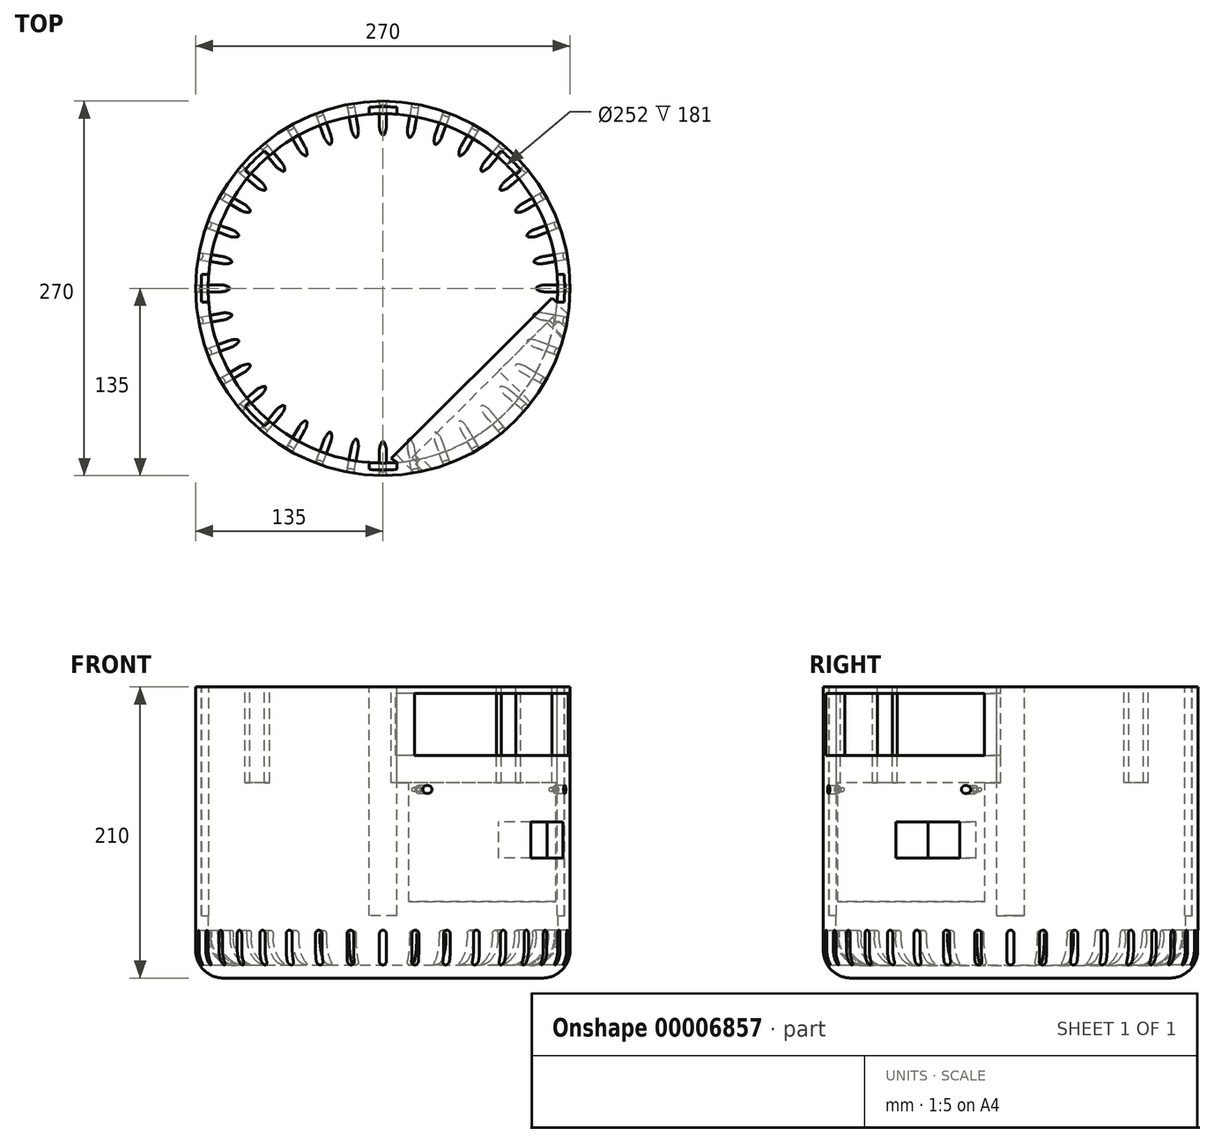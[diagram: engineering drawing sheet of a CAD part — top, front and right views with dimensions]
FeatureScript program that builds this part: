
annotation { "Feature Type Name" : "Feature", "Feature Type Description" : "" }
export const myFeature = defineFeature(function(context is Context, id is Id, definition is map)
    precondition{}
    {
        {
            var Q0;
            Q0=qCreatedBy(makeId("Top.planeOp"),FACE);
            var sketch = newSketch(context, id + "F0", { "sketchPlane" : qUnion([Q0])});
            skCircle(sketch, "E0", {"center": v(0, 0) * mm, "radius": 126 * mm});
            skCircle(sketch, "E1", {"center": v(0, 0) * mm, "radius": 135 * mm});
            skSolve(sketch);
        }
        {
            var Q0;
            Q0 = qSketchRegion(id + "F0", true);
            var Q1;
            Q1=makeQuery(id+"F0.imprint","IMPRINT",FACE,{"disambiguationData":[TD([[makeQuery(id+"F0.imprint","IMPRINT",EDGE,{"derivedFrom":sQuery(id+"F0.wireOp",EDGE,"ITGFbY2j-F6Gs-mvNy-kfQ0-MyUqCA95ELIB")}),-1.0]])]});
            var Q2;
            Q2=makeQuery(id+"F0.imprint","IMPRINT",FACE,{"disambiguationData":[TD([[makeQuery(id+"F0.imprint","IMPRINT",EDGE,{"derivedFrom":sQuery(id+"F0.wireOp",EDGE,"ITGFbY2j-F6Gs-mvNy-kfQ0-MyUqCA95ELIB")}),1.0]])]});
            var Q3;
            Q3=makeQuery(id+"F0.imprint","IMPRINT",FACE,{"disambiguationData":[TD([[makeQuery(id+"F0.imprint","IMPRINT",EDGE,{"derivedFrom":sQuery(id+"F0.wireOp",EDGE,"E0")}),1.0]])]});
            extrude(context, id + "F1", {"entities" : qUnion([Q0, Q1, Q2, Q3]), "oppositeDirection" : true, "depth" : 30 * mm});
        }
        {
            var Q0;
            Q0=makeQuery(id+"F0.imprint","IMPRINT",FACE,{"disambiguationData":[TD([[makeQuery(id+"F0.imprint","IMPRINT",EDGE,{"derivedFrom":sQuery(id+"F0.wireOp",EDGE,"E0")}),-1.0]])]});
            extrude(context, id + "F2", {"entities" : qUnion([Q0]), "operationType" : NewBodyOperationType.ADD, "depth" : 180 * mm});
        }
        {
            var Q0;
            Q0=makeQuery(id+"F1.opExtrude","CAP_FACE",FACE,{"disambiguationData":[OSD([sQuery(id+"F0.wireOp",EDGE,"E1")])],"isStart":true});
            shell(context, id + "F3", {"entities" : qUnion([Q0]), "thickness" : 9 * mm});
        }
        {
            var Q0;
            Q0=makeQuery(id+"F2.opExtrude","CAP_FACE",FACE,{"disambiguationData":[OSD([sQuery(id+"F0.wireOp",EDGE,"E0"),sQuery(id+"F0.wireOp",EDGE,"E1")])],"isStart":false});
            var sketch = newSketch(context, id + "F4", { "sketchPlane" : qUnion([Q0])});
            skCircle(sketch, "E2", {"center": v(0, 0) * mm, "radius": 126 * mm});
            skCircle(sketch, "E3", {"center": v(0, 0) * mm, "radius": 131 * mm});
            skLineSegment(sketch, "E4", {"start": v(-130.62, -10) * mm, "end": v(-125.6, -10) * mm});
            skLineSegment(sketch, "E5", {"start": v(-130.62, 10) * mm, "end": v(-125.6, 10) * mm});
            skLineSegment(sketch, "E6", {"start": v(125.6, 10) * mm, "end": v(130.62, 10) * mm});
            skLineSegment(sketch, "E7", {"start": v(125.6, -10) * mm, "end": v(130.62, -10) * mm});
            skLineSegment(sketch, "E8", {"start": v(-10, 125.6) * mm, "end": v(-10, 130.62) * mm});
            skLineSegment(sketch, "E9", {"start": v(10, 125.6) * mm, "end": v(10, 130.62) * mm});
            skPoint(sketch, "E10", {"position": v(0, 126) * mm});
            skPoint(sketch, "E11", {"position": v(-126, 0) * mm});
            skPoint(sketch, "E12", {"position": v(126, 0) * mm});
            skPoint(sketch, "E13", {"position": v(0, -126) * mm});
            skLineSegment(sketch, "E14", {"start": v(-128.11, 10) * mm, "end": v(-128.11, -10) * mm});
            skPoint(sketch, "E15", {"position": v(-128.11, 0) * mm});
            skLineSegment(sketch, "E16", {"start": v(164.04, 10) * mm, "end": v(164.04, -10) * mm});
            skPoint(sketch, "E17", {"position": v(164.04, 0) * mm});
            skLineSegment(sketch, "E18", {"start": v(-10, -125.6) * mm, "end": v(-10, -130.62) * mm});
            skLineSegment(sketch, "E19", {"start": v(10, -125.6) * mm, "end": v(10, -130.62) * mm});
            skLineSegment(sketch, "E20", {"start": v(-10, -126.16) * mm, "end": v(10, -126.16) * mm});
            skPoint(sketch, "E21", {"position": v(0, -126.16) * mm});
            skLineSegment(sketch, "E22", {"start": v(-10, 175.22) * mm, "end": v(10, 175.22) * mm});
            skPoint(sketch, "E23", {"position": v(0, 175.22) * mm});
            skLineSegment(sketch, "E24", {"start": v(0, 0) * mm, "end": v(0, 71.25) * mm});
            skLineSegment(sketch, "E25", {"start": v(23.85, 0) * mm, "end": v(0, 0) * mm});
            skLineSegment(sketch, "E26", {"start": v(-90.59, 90.59) * mm, "end": v(90.59, -90.59) * mm});
            skLineSegment(sketch, "E27", {"start": v(-43.26, -43.26) * mm, "end": v(90.59, 90.59) * mm});
            skLineSegment(sketch, "E28", {"start": v(81.74, 95.89) * mm, "end": v(85.29, 99.43) * mm});
            skLineSegment(sketch, "E29", {"start": v(95.89, 81.74) * mm, "end": v(99.43, 85.29) * mm});
            skLineSegment(sketch, "E30", {"start": v(83.52, 97.66) * mm, "end": v(97.66, 83.52) * mm});
            skPoint(sketch, "E31", {"position": v(90.59, 90.59) * mm});
            skLineSegment(sketch, "E32", {"start": v(-99.43, -85.29) * mm, "end": v(-95.89, -81.74) * mm});
            skLineSegment(sketch, "E33", {"start": v(-85.29, -99.43) * mm, "end": v(-81.74, -95.89) * mm});
            skLineSegment(sketch, "E34", {"start": v(-50.33, -36.19) * mm, "end": v(-36.19, -50.33) * mm});
            skPoint(sketch, "E35", {"position": v(-43.26, -43.26) * mm});
            skLineSegment(sketch, "E36", {"start": v(95.89, -81.74) * mm, "end": v(99.43, -85.29) * mm});
            skLineSegment(sketch, "E37", {"start": v(81.74, -95.89) * mm, "end": v(85.29, -99.43) * mm});
            skLineSegment(sketch, "E38", {"start": v(83.52, -97.66) * mm, "end": v(97.66, -83.52) * mm});
            skPoint(sketch, "E39", {"position": v(90.59, -90.59) * mm});
            skLineSegment(sketch, "E40", {"start": v(-85.29, 99.43) * mm, "end": v(-81.74, 95.89) * mm});
            skLineSegment(sketch, "E41", {"start": v(-99.43, 85.29) * mm, "end": v(-95.89, 81.74) * mm});
            skLineSegment(sketch, "E42", {"start": v(-97.66, 83.52) * mm, "end": v(-83.52, 97.66) * mm});
            skPoint(sketch, "E43", {"position": v(-90.59, 90.59) * mm});
            skSolve(sketch);
        }
        {
            var Q0;
            {var subQ5=sQuery(id+"F4.wireOp",EDGE,"E14");Q0=makeQuery(id+"F4.imprint","IMPRINT",FACE,{"disambiguationData":[TD([[makeQuery(id+"F4.imprint","IMPRINT",EDGE,{"derivedFrom":subQ5}),-1.0]])]});}
            var Q1;
            {var subQ5=sQuery(id+"F4.wireOp",EDGE,"E14");Q1=makeQuery(id+"F4.imprint","IMPRINT",FACE,{"disambiguationData":[TD([[makeQuery(id+"F4.imprint","IMPRINT",EDGE,{"derivedFrom":subQ5}),1.0]])]});}
            var Q2;
            {var subQ5=sQuery(id+"F4.wireOp",EDGE,"E22");Q2=makeQuery(id+"F4.imprint","IMPRINT",FACE,{"disambiguationData":[TD([[makeQuery(id+"F4.imprint","IMPRINT",EDGE,{"derivedFrom":subQ5}),-1.0]])]});}
            var Q3;
            {var subQ5=sQuery(id+"F4.wireOp",EDGE,"E22");Q3=makeQuery(id+"F4.imprint","IMPRINT",FACE,{"disambiguationData":[TD([[makeQuery(id+"F4.imprint","IMPRINT",EDGE,{"derivedFrom":subQ5}),1.0]])]});}
            var Q4;
            {var subQ5=sQuery(id+"F4.wireOp",EDGE,"E16");Q4=makeQuery(id+"F4.imprint","IMPRINT",FACE,{"disambiguationData":[TD([[makeQuery(id+"F4.imprint","IMPRINT",EDGE,{"derivedFrom":subQ5}),1.0]])]});}
            var Q5;
            {var subQ5=sQuery(id+"F4.wireOp",EDGE,"E20");Q5=makeQuery(id+"F4.imprint","IMPRINT",FACE,{"disambiguationData":[TD([[makeQuery(id+"F4.imprint","IMPRINT",EDGE,{"derivedFrom":subQ5}),-1.0]])]});}
            var Q6;
            {var subQ5=sQuery(id+"F4.wireOp",EDGE,"E20");Q6=makeQuery(id+"F4.imprint","IMPRINT",FACE,{"disambiguationData":[TD([[makeQuery(id+"F4.imprint","IMPRINT",EDGE,{"derivedFrom":subQ5}),1.0]])]});}
            var Q7;
            {var subQ5=sQuery(id+"F4.wireOp",EDGE,"E16");Q7=makeQuery(id+"F4.imprint","IMPRINT",FACE,{"disambiguationData":[TD([[makeQuery(id+"F4.imprint","IMPRINT",EDGE,{"derivedFrom":subQ5}),-1.0]])]});}
            var Q8;
            {var subQ0=sQuery(id+"F4.wireOp",EDGE,"E6");Q8=makeQuery(id+"F4.imprint","IMPRINT",FACE,{"disambiguationData":[TD([[makeQuery(id+"F4.imprint","IMPRINT",EDGE,{"derivedFrom":subQ0}),-1.0]])]});}
            var Q9;
            {var subQ0=sQuery(id+"F4.wireOp",EDGE,"E8");Q9=makeQuery(id+"F4.imprint","IMPRINT",FACE,{"disambiguationData":[TD([[makeQuery(id+"F4.imprint","IMPRINT",EDGE,{"derivedFrom":subQ0}),-1.0]])]});}
            extrude(context, id + "F5", {"entities" : qUnion([Q0, Q1, Q2, Q3, Q4, Q5, Q6, Q7, Q8, Q9]), "operationType" : NewBodyOperationType.REMOVE, "oppositeDirection" : true, "depth" : 165 * mm});
        }
        {
            var Q0;
            {var subQ4=sQuery(id+"F4.wireOp",EDGE,"E3");var subQ6=sQuery(id+"F4.wireOp",EDGE,"E40");var subQ7=makeQuery(id+"F4.imprint","INTERSECT",VERTEX,{"derivedFrom":[subQ4,subQ6]});Q0=makeQuery(id+"F4.imprint","IMPRINT",FACE,{"disambiguationData":[TD([[makeQuery(id+"F4.imprint","IMPRINT",EDGE,{"disambiguationData":[TD([[subQ7,-1.0]])],"derivedFrom":subQ4}),1.0]])]});}
            var Q1;
            {var subQ0=sQuery(id+"F4.wireOp",EDGE,"E41");var subQ1=sQuery(id+"F4.wireOp",EDGE,"E2");var subQ2=makeQuery(id+"F4.imprint","INTERSECT",VERTEX,{"derivedFrom":[subQ1,subQ0]});Q1=makeQuery(id+"F4.imprint","IMPRINT",FACE,{"disambiguationData":[TD([[makeQuery(id+"F4.imprint","IMPRINT",EDGE,{"disambiguationData":[TD([[subQ2,1.0]])],"derivedFrom":subQ1}),-1.0]])]});}
            var Q2;
            {var subQ0=sQuery(id+"F4.wireOp",EDGE,"E40");var subQ1=sQuery(id+"F4.wireOp",EDGE,"E2");var subQ2=makeQuery(id+"F4.imprint","INTERSECT",VERTEX,{"derivedFrom":[subQ1,subQ0]});Q2=makeQuery(id+"F4.imprint","IMPRINT",FACE,{"disambiguationData":[TD([[makeQuery(id+"F4.imprint","IMPRINT",EDGE,{"disambiguationData":[TD([[subQ2,-1.0]])],"derivedFrom":subQ1}),-1.0]])]});}
            var Q3;
            {var subQ2=sQuery(id+"F4.wireOp",EDGE,"E28");var subQ5=sQuery(id+"F4.wireOp",EDGE,"E3");var subQ8=makeQuery(id+"F4.imprint","INTERSECT",VERTEX,{"derivedFrom":[subQ5,subQ2]});Q3=makeQuery(id+"F4.imprint","IMPRINT",FACE,{"disambiguationData":[TD([[makeQuery(id+"F4.imprint","IMPRINT",EDGE,{"disambiguationData":[TD([[subQ8,1.0]])],"derivedFrom":subQ5}),1.0]])]});}
            var Q4;
            {var subQ0=sQuery(id+"F4.wireOp",EDGE,"E28");var subQ1=sQuery(id+"F4.wireOp",EDGE,"E2");var subQ2=makeQuery(id+"F4.imprint","INTERSECT",VERTEX,{"derivedFrom":[subQ1,subQ0]});Q4=makeQuery(id+"F4.imprint","IMPRINT",FACE,{"disambiguationData":[TD([[makeQuery(id+"F4.imprint","IMPRINT",EDGE,{"disambiguationData":[TD([[subQ2,1.0]])],"derivedFrom":subQ1}),-1.0]])]});}
            var Q5;
            {var subQ0=sQuery(id+"F4.wireOp",EDGE,"E29");var subQ1=sQuery(id+"F4.wireOp",EDGE,"E2");var subQ2=makeQuery(id+"F4.imprint","INTERSECT",VERTEX,{"derivedFrom":[subQ1,subQ0]});Q5=makeQuery(id+"F4.imprint","IMPRINT",FACE,{"disambiguationData":[TD([[makeQuery(id+"F4.imprint","IMPRINT",EDGE,{"disambiguationData":[TD([[subQ2,-1.0]])],"derivedFrom":subQ1}),-1.0]])]});}
            var Q6;
            {var subQ0=sQuery(id+"F4.wireOp",EDGE,"E36");var subQ1=sQuery(id+"F4.wireOp",EDGE,"E2");var subQ2=makeQuery(id+"F4.imprint","INTERSECT",VERTEX,{"derivedFrom":[subQ1,subQ0]});Q6=makeQuery(id+"F4.imprint","IMPRINT",FACE,{"disambiguationData":[TD([[makeQuery(id+"F4.imprint","IMPRINT",EDGE,{"disambiguationData":[TD([[subQ2,1.0]])],"derivedFrom":subQ1}),-1.0]])]});}
            var Q7;
            {var subQ0=sQuery(id+"F4.wireOp",EDGE,"E37");var subQ1=sQuery(id+"F4.wireOp",EDGE,"E2");var subQ2=makeQuery(id+"F4.imprint","INTERSECT",VERTEX,{"derivedFrom":[subQ1,subQ0]});Q7=makeQuery(id+"F4.imprint","IMPRINT",FACE,{"disambiguationData":[TD([[makeQuery(id+"F4.imprint","IMPRINT",EDGE,{"disambiguationData":[TD([[subQ2,-1.0]])],"derivedFrom":subQ1}),-1.0]])]});}
            var Q8;
            {var subQ1=sQuery(id+"F4.wireOp",EDGE,"E3");var subQ6=sQuery(id+"F4.wireOp",EDGE,"E36");var subQ7=makeQuery(id+"F4.imprint","INTERSECT",VERTEX,{"derivedFrom":[subQ1,subQ6]});Q8=makeQuery(id+"F4.imprint","IMPRINT",FACE,{"disambiguationData":[TD([[makeQuery(id+"F4.imprint","IMPRINT",EDGE,{"disambiguationData":[TD([[subQ7,1.0]])],"derivedFrom":subQ1}),1.0]])]});}
            var Q9;
            {var subQ0=sQuery(id+"F4.wireOp",EDGE,"E33");var subQ1=sQuery(id+"F4.wireOp",EDGE,"E2");var subQ2=makeQuery(id+"F4.imprint","INTERSECT",VERTEX,{"derivedFrom":[subQ1,subQ0]});Q9=makeQuery(id+"F4.imprint","IMPRINT",FACE,{"disambiguationData":[TD([[makeQuery(id+"F4.imprint","IMPRINT",EDGE,{"disambiguationData":[TD([[subQ2,1.0]])],"derivedFrom":subQ1}),-1.0]])]});}
            var Q10;
            {var subQ0=sQuery(id+"F4.wireOp",EDGE,"E32");var subQ1=sQuery(id+"F4.wireOp",EDGE,"E2");var subQ2=makeQuery(id+"F4.imprint","INTERSECT",VERTEX,{"derivedFrom":[subQ1,subQ0]});Q10=makeQuery(id+"F4.imprint","IMPRINT",FACE,{"disambiguationData":[TD([[makeQuery(id+"F4.imprint","IMPRINT",EDGE,{"disambiguationData":[TD([[subQ2,-1.0]])],"derivedFrom":subQ1}),-1.0]])]});}
            var Q11;
            {var subQ1=sQuery(id+"F4.wireOp",EDGE,"E3");var subQ5=sQuery(id+"F4.wireOp",EDGE,"E32");var subQ6=makeQuery(id+"F4.imprint","INTERSECT",VERTEX,{"derivedFrom":[subQ1,subQ5]});Q11=makeQuery(id+"F4.imprint","IMPRINT",FACE,{"disambiguationData":[TD([[makeQuery(id+"F4.imprint","IMPRINT",EDGE,{"disambiguationData":[TD([[subQ6,-1.0]])],"derivedFrom":subQ1}),1.0]])]});}
            extrude(context, id + "F6", {"entities" : qUnion([Q0, Q1, Q2, Q3, Q4, Q5, Q6, Q7, Q8, Q9, Q10, Q11]), "operationType" : NewBodyOperationType.REMOVE, "oppositeDirection" : true, "depth" : 69 * mm});
        }
        {
            var Q0;
            Q0=qCreatedBy(makeId("Front.planeOp"),FACE);
            cPlane(context, id + "F7", {"entities" : qUnion([Q0]), "cplaneType" : CPlaneType.OFFSET, "offset" : 120 * mm, "width" : 150 * mm, "height" : 150 * mm});
        }
        {
            var Q0;
            Q0=qCreatedBy(id+"F7.planeOp",FACE);
            var sketch = newSketch(context, id + "F8", { "sketchPlane" : qUnion([Q0])});
            skLineSegment(sketch, "E44.bottom", {"start": v(-2.5, -18) * mm, "end": v(2.5, -18) * mm});
            skLineSegment(sketch, "E44.top", {"start": v(-2.5, 2) * mm, "end": v(2.5, 2) * mm});
            skLineSegment(sketch, "E44.left", {"start": v(-2.5, -18) * mm, "end": v(-2.5, 2) * mm});
            skLineSegment(sketch, "E44.right", {"start": v(2.5, -18) * mm, "end": v(2.5, 2) * mm});
            skPoint(sketch, "E45", {"position": v(0, 2) * mm});
            skPoint(sketch, "E45.positionSnap0", {"position": v(0, 2) * mm});
            skPoint(sketch, "E46", {"position": v(0, 0) * mm});
            skArc(sketch, "E47", {"start": v(2.5, 2) * mm, "mid": v(0, 4.5) * mm, "end": v(-2.5, 2) * mm});
            skArc(sketch, "E48", {"start": v(-2.5, -18) * mm, "mid": v(0, -20.5) * mm, "end": v(2.5, -18) * mm});
            skSolve(sketch);
        }
        {
            var Q0;
            Q0 = qSketchRegion(id + "F8", true);
            extrude(context, id + "F9", {"entities" : qUnion([Q0]), "depth" : 25 * mm});
        }
        {
            var Q0;
            Q0=makeQuery(id+"F9.opExtrude","SWEPT_BODY",BODY,{"disambiguationData":[OSD([sQuery(id+"F8.wireOp",EDGE,"E44.bottom"),sQuery(id+"F8.wireOp",EDGE,"E44.top"),sQuery(id+"F8.wireOp",EDGE,"E44.left"),sQuery(id+"F8.wireOp",EDGE,"E44.right")])]});
            var Q1;
            Q1=makeQuery(id+"F2.opExtrude","CAP_EDGE",EDGE,{"disambiguationData":[OSD([sQuery(id+"F0.wireOp",EDGE,"E1")])],"isStart":false});
            circularPattern(context, id + "F10", {"entities" : qUnion([Q0]), "axis" : qUnion([Q1]), "angle" : 10 * degree, "instanceCount" : 40});
        }
        {
            var Q0;
            Q0=makeQuery(id+"F9.opExtrude","SWEPT_BODY",BODY,{"disambiguationData":[OSD([sQuery(id+"F8.wireOp",EDGE,"E44.bottom"),sQuery(id+"F8.wireOp",EDGE,"E44.top"),sQuery(id+"F8.wireOp",EDGE,"E44.left"),sQuery(id+"F8.wireOp",EDGE,"E44.right")])]});
            var Q1;
            Q1=makeQuery(id+"F10.opPattern","COPY",BODY,{"derivedFrom":makeQuery(id+"F9.opExtrude","SWEPT_BODY",BODY,{"disambiguationData":[OSD([sQuery(id+"F8.wireOp",EDGE,"E44.bottom"),sQuery(id+"F8.wireOp",EDGE,"E44.top"),sQuery(id+"F8.wireOp",EDGE,"E44.left"),sQuery(id+"F8.wireOp",EDGE,"E44.right")])]}),"instanceName":"1"});
            var Q2;
            Q2=makeQuery(id+"F10.opPattern","COPY",BODY,{"derivedFrom":makeQuery(id+"F9.opExtrude","SWEPT_BODY",BODY,{"disambiguationData":[OSD([sQuery(id+"F8.wireOp",EDGE,"E44.bottom"),sQuery(id+"F8.wireOp",EDGE,"E44.top"),sQuery(id+"F8.wireOp",EDGE,"E44.left"),sQuery(id+"F8.wireOp",EDGE,"E44.right")])]}),"instanceName":"2"});
            var Q3;
            Q3=makeQuery(id+"F10.opPattern","COPY",BODY,{"derivedFrom":makeQuery(id+"F9.opExtrude","SWEPT_BODY",BODY,{"disambiguationData":[OSD([sQuery(id+"F8.wireOp",EDGE,"E44.bottom"),sQuery(id+"F8.wireOp",EDGE,"E44.top"),sQuery(id+"F8.wireOp",EDGE,"E44.left"),sQuery(id+"F8.wireOp",EDGE,"E44.right")])]}),"instanceName":"3"});
            var Q4;
            Q4=makeQuery(id+"F10.opPattern","COPY",BODY,{"derivedFrom":makeQuery(id+"F9.opExtrude","SWEPT_BODY",BODY,{"disambiguationData":[OSD([sQuery(id+"F8.wireOp",EDGE,"E44.bottom"),sQuery(id+"F8.wireOp",EDGE,"E44.top"),sQuery(id+"F8.wireOp",EDGE,"E44.left"),sQuery(id+"F8.wireOp",EDGE,"E44.right")])]}),"instanceName":"4"});
            var Q5;
            Q5=makeQuery(id+"F10.opPattern","COPY",BODY,{"derivedFrom":makeQuery(id+"F9.opExtrude","SWEPT_BODY",BODY,{"disambiguationData":[OSD([sQuery(id+"F8.wireOp",EDGE,"E44.bottom"),sQuery(id+"F8.wireOp",EDGE,"E44.top"),sQuery(id+"F8.wireOp",EDGE,"E44.left"),sQuery(id+"F8.wireOp",EDGE,"E44.right")])]}),"instanceName":"5"});
            var Q6;
            Q6=makeQuery(id+"F10.opPattern","COPY",BODY,{"derivedFrom":makeQuery(id+"F9.opExtrude","SWEPT_BODY",BODY,{"disambiguationData":[OSD([sQuery(id+"F8.wireOp",EDGE,"E44.bottom"),sQuery(id+"F8.wireOp",EDGE,"E44.top"),sQuery(id+"F8.wireOp",EDGE,"E44.left"),sQuery(id+"F8.wireOp",EDGE,"E44.right")])]}),"instanceName":"6"});
            var Q7;
            Q7=makeQuery(id+"F10.opPattern","COPY",BODY,{"derivedFrom":makeQuery(id+"F9.opExtrude","SWEPT_BODY",BODY,{"disambiguationData":[OSD([sQuery(id+"F8.wireOp",EDGE,"E44.bottom"),sQuery(id+"F8.wireOp",EDGE,"E44.top"),sQuery(id+"F8.wireOp",EDGE,"E44.left"),sQuery(id+"F8.wireOp",EDGE,"E44.right")])]}),"instanceName":"7"});
            var Q8;
            Q8=makeQuery(id+"F10.opPattern","COPY",BODY,{"derivedFrom":makeQuery(id+"F9.opExtrude","SWEPT_BODY",BODY,{"disambiguationData":[OSD([sQuery(id+"F8.wireOp",EDGE,"E44.bottom"),sQuery(id+"F8.wireOp",EDGE,"E44.top"),sQuery(id+"F8.wireOp",EDGE,"E44.left"),sQuery(id+"F8.wireOp",EDGE,"E44.right")])]}),"instanceName":"8"});
            var Q9;
            Q9=makeQuery(id+"F10.opPattern","COPY",BODY,{"derivedFrom":makeQuery(id+"F9.opExtrude","SWEPT_BODY",BODY,{"disambiguationData":[OSD([sQuery(id+"F8.wireOp",EDGE,"E44.bottom"),sQuery(id+"F8.wireOp",EDGE,"E44.top"),sQuery(id+"F8.wireOp",EDGE,"E44.left"),sQuery(id+"F8.wireOp",EDGE,"E44.right")])]}),"instanceName":"9"});
            var Q10;
            Q10=makeQuery(id+"F10.opPattern","COPY",BODY,{"derivedFrom":makeQuery(id+"F9.opExtrude","SWEPT_BODY",BODY,{"disambiguationData":[OSD([sQuery(id+"F8.wireOp",EDGE,"E44.bottom"),sQuery(id+"F8.wireOp",EDGE,"E44.top"),sQuery(id+"F8.wireOp",EDGE,"E44.left"),sQuery(id+"F8.wireOp",EDGE,"E44.right")])]}),"instanceName":"10"});
            var Q11;
            Q11=makeQuery(id+"F10.opPattern","COPY",BODY,{"derivedFrom":makeQuery(id+"F9.opExtrude","SWEPT_BODY",BODY,{"disambiguationData":[OSD([sQuery(id+"F8.wireOp",EDGE,"E44.bottom"),sQuery(id+"F8.wireOp",EDGE,"E44.top"),sQuery(id+"F8.wireOp",EDGE,"E44.left"),sQuery(id+"F8.wireOp",EDGE,"E44.right")])]}),"instanceName":"11"});
            var Q12;
            Q12=makeQuery(id+"F10.opPattern","COPY",BODY,{"derivedFrom":makeQuery(id+"F9.opExtrude","SWEPT_BODY",BODY,{"disambiguationData":[OSD([sQuery(id+"F8.wireOp",EDGE,"E44.bottom"),sQuery(id+"F8.wireOp",EDGE,"E44.top"),sQuery(id+"F8.wireOp",EDGE,"E44.left"),sQuery(id+"F8.wireOp",EDGE,"E44.right")])]}),"instanceName":"12"});
            var Q13;
            Q13=makeQuery(id+"F10.opPattern","COPY",BODY,{"derivedFrom":makeQuery(id+"F9.opExtrude","SWEPT_BODY",BODY,{"disambiguationData":[OSD([sQuery(id+"F8.wireOp",EDGE,"E44.bottom"),sQuery(id+"F8.wireOp",EDGE,"E44.top"),sQuery(id+"F8.wireOp",EDGE,"E44.left"),sQuery(id+"F8.wireOp",EDGE,"E44.right")])]}),"instanceName":"13"});
            var Q14;
            Q14=makeQuery(id+"F10.opPattern","COPY",BODY,{"derivedFrom":makeQuery(id+"F9.opExtrude","SWEPT_BODY",BODY,{"disambiguationData":[OSD([sQuery(id+"F8.wireOp",EDGE,"E44.bottom"),sQuery(id+"F8.wireOp",EDGE,"E44.top"),sQuery(id+"F8.wireOp",EDGE,"E44.left"),sQuery(id+"F8.wireOp",EDGE,"E44.right")])]}),"instanceName":"14"});
            var Q15;
            Q15=makeQuery(id+"F10.opPattern","COPY",BODY,{"derivedFrom":makeQuery(id+"F9.opExtrude","SWEPT_BODY",BODY,{"disambiguationData":[OSD([sQuery(id+"F8.wireOp",EDGE,"E44.bottom"),sQuery(id+"F8.wireOp",EDGE,"E44.top"),sQuery(id+"F8.wireOp",EDGE,"E44.left"),sQuery(id+"F8.wireOp",EDGE,"E44.right")])]}),"instanceName":"15"});
            var Q16;
            Q16=makeQuery(id+"F10.opPattern","COPY",BODY,{"derivedFrom":makeQuery(id+"F9.opExtrude","SWEPT_BODY",BODY,{"disambiguationData":[OSD([sQuery(id+"F8.wireOp",EDGE,"E44.bottom"),sQuery(id+"F8.wireOp",EDGE,"E44.top"),sQuery(id+"F8.wireOp",EDGE,"E44.left"),sQuery(id+"F8.wireOp",EDGE,"E44.right")])]}),"instanceName":"16"});
            var Q17;
            Q17=makeQuery(id+"F10.opPattern","COPY",BODY,{"derivedFrom":makeQuery(id+"F9.opExtrude","SWEPT_BODY",BODY,{"disambiguationData":[OSD([sQuery(id+"F8.wireOp",EDGE,"E44.bottom"),sQuery(id+"F8.wireOp",EDGE,"E44.top"),sQuery(id+"F8.wireOp",EDGE,"E44.left"),sQuery(id+"F8.wireOp",EDGE,"E44.right")])]}),"instanceName":"17"});
            var Q18;
            Q18=makeQuery(id+"F10.opPattern","COPY",BODY,{"derivedFrom":makeQuery(id+"F9.opExtrude","SWEPT_BODY",BODY,{"disambiguationData":[OSD([sQuery(id+"F8.wireOp",EDGE,"E44.bottom"),sQuery(id+"F8.wireOp",EDGE,"E44.top"),sQuery(id+"F8.wireOp",EDGE,"E44.left"),sQuery(id+"F8.wireOp",EDGE,"E44.right")])]}),"instanceName":"18"});
            var Q19;
            Q19=makeQuery(id+"F10.opPattern","COPY",BODY,{"derivedFrom":makeQuery(id+"F9.opExtrude","SWEPT_BODY",BODY,{"disambiguationData":[OSD([sQuery(id+"F8.wireOp",EDGE,"E44.bottom"),sQuery(id+"F8.wireOp",EDGE,"E44.top"),sQuery(id+"F8.wireOp",EDGE,"E44.left"),sQuery(id+"F8.wireOp",EDGE,"E44.right")])]}),"instanceName":"19"});
            var Q20;
            Q20=makeQuery(id+"F10.opPattern","COPY",BODY,{"derivedFrom":makeQuery(id+"F9.opExtrude","SWEPT_BODY",BODY,{"disambiguationData":[OSD([sQuery(id+"F8.wireOp",EDGE,"E44.bottom"),sQuery(id+"F8.wireOp",EDGE,"E44.top"),sQuery(id+"F8.wireOp",EDGE,"E44.left"),sQuery(id+"F8.wireOp",EDGE,"E44.right")])]}),"instanceName":"20"});
            var Q21;
            Q21=makeQuery(id+"F10.opPattern","COPY",BODY,{"derivedFrom":makeQuery(id+"F9.opExtrude","SWEPT_BODY",BODY,{"disambiguationData":[OSD([sQuery(id+"F8.wireOp",EDGE,"E44.bottom"),sQuery(id+"F8.wireOp",EDGE,"E44.top"),sQuery(id+"F8.wireOp",EDGE,"E44.left"),sQuery(id+"F8.wireOp",EDGE,"E44.right")])]}),"instanceName":"21"});
            var Q22;
            Q22=makeQuery(id+"F10.opPattern","COPY",BODY,{"derivedFrom":makeQuery(id+"F9.opExtrude","SWEPT_BODY",BODY,{"disambiguationData":[OSD([sQuery(id+"F8.wireOp",EDGE,"E44.bottom"),sQuery(id+"F8.wireOp",EDGE,"E44.top"),sQuery(id+"F8.wireOp",EDGE,"E44.left"),sQuery(id+"F8.wireOp",EDGE,"E44.right")])]}),"instanceName":"22"});
            var Q23;
            Q23=makeQuery(id+"F10.opPattern","COPY",BODY,{"derivedFrom":makeQuery(id+"F9.opExtrude","SWEPT_BODY",BODY,{"disambiguationData":[OSD([sQuery(id+"F8.wireOp",EDGE,"E44.bottom"),sQuery(id+"F8.wireOp",EDGE,"E44.top"),sQuery(id+"F8.wireOp",EDGE,"E44.left"),sQuery(id+"F8.wireOp",EDGE,"E44.right")])]}),"instanceName":"23"});
            var Q24;
            Q24=makeQuery(id+"F10.opPattern","COPY",BODY,{"derivedFrom":makeQuery(id+"F9.opExtrude","SWEPT_BODY",BODY,{"disambiguationData":[OSD([sQuery(id+"F8.wireOp",EDGE,"E44.bottom"),sQuery(id+"F8.wireOp",EDGE,"E44.top"),sQuery(id+"F8.wireOp",EDGE,"E44.left"),sQuery(id+"F8.wireOp",EDGE,"E44.right")])]}),"instanceName":"24"});
            var Q25;
            Q25=makeQuery(id+"F10.opPattern","COPY",BODY,{"derivedFrom":makeQuery(id+"F9.opExtrude","SWEPT_BODY",BODY,{"disambiguationData":[OSD([sQuery(id+"F8.wireOp",EDGE,"E44.bottom"),sQuery(id+"F8.wireOp",EDGE,"E44.top"),sQuery(id+"F8.wireOp",EDGE,"E44.left"),sQuery(id+"F8.wireOp",EDGE,"E44.right")])]}),"instanceName":"25"});
            var Q26;
            Q26=makeQuery(id+"F10.opPattern","COPY",BODY,{"derivedFrom":makeQuery(id+"F9.opExtrude","SWEPT_BODY",BODY,{"disambiguationData":[OSD([sQuery(id+"F8.wireOp",EDGE,"E44.bottom"),sQuery(id+"F8.wireOp",EDGE,"E44.top"),sQuery(id+"F8.wireOp",EDGE,"E44.left"),sQuery(id+"F8.wireOp",EDGE,"E44.right")])]}),"instanceName":"26"});
            var Q27;
            Q27=makeQuery(id+"F10.opPattern","COPY",BODY,{"derivedFrom":makeQuery(id+"F9.opExtrude","SWEPT_BODY",BODY,{"disambiguationData":[OSD([sQuery(id+"F8.wireOp",EDGE,"E44.bottom"),sQuery(id+"F8.wireOp",EDGE,"E44.top"),sQuery(id+"F8.wireOp",EDGE,"E44.left"),sQuery(id+"F8.wireOp",EDGE,"E44.right")])]}),"instanceName":"27"});
            var Q28;
            Q28=makeQuery(id+"F10.opPattern","COPY",BODY,{"derivedFrom":makeQuery(id+"F9.opExtrude","SWEPT_BODY",BODY,{"disambiguationData":[OSD([sQuery(id+"F8.wireOp",EDGE,"E44.bottom"),sQuery(id+"F8.wireOp",EDGE,"E44.top"),sQuery(id+"F8.wireOp",EDGE,"E44.left"),sQuery(id+"F8.wireOp",EDGE,"E44.right")])]}),"instanceName":"28"});
            var Q29;
            Q29=makeQuery(id+"F10.opPattern","COPY",BODY,{"derivedFrom":makeQuery(id+"F9.opExtrude","SWEPT_BODY",BODY,{"disambiguationData":[OSD([sQuery(id+"F8.wireOp",EDGE,"E44.bottom"),sQuery(id+"F8.wireOp",EDGE,"E44.top"),sQuery(id+"F8.wireOp",EDGE,"E44.left"),sQuery(id+"F8.wireOp",EDGE,"E44.right")])]}),"instanceName":"29"});
            var Q30;
            Q30=makeQuery(id+"F10.opPattern","COPY",BODY,{"derivedFrom":makeQuery(id+"F9.opExtrude","SWEPT_BODY",BODY,{"disambiguationData":[OSD([sQuery(id+"F8.wireOp",EDGE,"E44.bottom"),sQuery(id+"F8.wireOp",EDGE,"E44.top"),sQuery(id+"F8.wireOp",EDGE,"E44.left"),sQuery(id+"F8.wireOp",EDGE,"E44.right")])]}),"instanceName":"30"});
            var Q31;
            Q31=makeQuery(id+"F10.opPattern","COPY",BODY,{"derivedFrom":makeQuery(id+"F9.opExtrude","SWEPT_BODY",BODY,{"disambiguationData":[OSD([sQuery(id+"F8.wireOp",EDGE,"E44.bottom"),sQuery(id+"F8.wireOp",EDGE,"E44.top"),sQuery(id+"F8.wireOp",EDGE,"E44.left"),sQuery(id+"F8.wireOp",EDGE,"E44.right")])]}),"instanceName":"31"});
            var Q32;
            Q32=makeQuery(id+"F10.opPattern","COPY",BODY,{"derivedFrom":makeQuery(id+"F9.opExtrude","SWEPT_BODY",BODY,{"disambiguationData":[OSD([sQuery(id+"F8.wireOp",EDGE,"E44.bottom"),sQuery(id+"F8.wireOp",EDGE,"E44.top"),sQuery(id+"F8.wireOp",EDGE,"E44.left"),sQuery(id+"F8.wireOp",EDGE,"E44.right")])]}),"instanceName":"32"});
            var Q33;
            Q33=makeQuery(id+"F10.opPattern","COPY",BODY,{"derivedFrom":makeQuery(id+"F9.opExtrude","SWEPT_BODY",BODY,{"disambiguationData":[OSD([sQuery(id+"F8.wireOp",EDGE,"E44.bottom"),sQuery(id+"F8.wireOp",EDGE,"E44.top"),sQuery(id+"F8.wireOp",EDGE,"E44.left"),sQuery(id+"F8.wireOp",EDGE,"E44.right")])]}),"instanceName":"33"});
            var Q34;
            Q34=makeQuery(id+"F10.opPattern","COPY",BODY,{"derivedFrom":makeQuery(id+"F9.opExtrude","SWEPT_BODY",BODY,{"disambiguationData":[OSD([sQuery(id+"F8.wireOp",EDGE,"E44.bottom"),sQuery(id+"F8.wireOp",EDGE,"E44.top"),sQuery(id+"F8.wireOp",EDGE,"E44.left"),sQuery(id+"F8.wireOp",EDGE,"E44.right")])]}),"instanceName":"34"});
            var Q35;
            Q35=makeQuery(id+"F10.opPattern","COPY",BODY,{"derivedFrom":makeQuery(id+"F9.opExtrude","SWEPT_BODY",BODY,{"disambiguationData":[OSD([sQuery(id+"F8.wireOp",EDGE,"E44.bottom"),sQuery(id+"F8.wireOp",EDGE,"E44.top"),sQuery(id+"F8.wireOp",EDGE,"E44.left"),sQuery(id+"F8.wireOp",EDGE,"E44.right")])]}),"instanceName":"35"});
            var Q36;
            Q36=makeQuery(id+"F10.opPattern","COPY",BODY,{"derivedFrom":makeQuery(id+"F9.opExtrude","SWEPT_BODY",BODY,{"disambiguationData":[OSD([sQuery(id+"F8.wireOp",EDGE,"E44.bottom"),sQuery(id+"F8.wireOp",EDGE,"E44.top"),sQuery(id+"F8.wireOp",EDGE,"E44.left"),sQuery(id+"F8.wireOp",EDGE,"E44.right")])]}),"instanceName":"36"});
            var Q37;
            Q37=makeQuery(id+"F10.opPattern","COPY",BODY,{"derivedFrom":makeQuery(id+"F9.opExtrude","SWEPT_BODY",BODY,{"disambiguationData":[OSD([sQuery(id+"F8.wireOp",EDGE,"E44.bottom"),sQuery(id+"F8.wireOp",EDGE,"E44.top"),sQuery(id+"F8.wireOp",EDGE,"E44.left"),sQuery(id+"F8.wireOp",EDGE,"E44.right")])]}),"instanceName":"37"});
            var Q38;
            Q38=makeQuery(id+"F10.opPattern","COPY",BODY,{"derivedFrom":makeQuery(id+"F9.opExtrude","SWEPT_BODY",BODY,{"disambiguationData":[OSD([sQuery(id+"F8.wireOp",EDGE,"E44.bottom"),sQuery(id+"F8.wireOp",EDGE,"E44.top"),sQuery(id+"F8.wireOp",EDGE,"E44.left"),sQuery(id+"F8.wireOp",EDGE,"E44.right")])]}),"instanceName":"38"});
            var Q39;
            Q39=makeQuery(id+"F10.opPattern","COPY",BODY,{"derivedFrom":makeQuery(id+"F9.opExtrude","SWEPT_BODY",BODY,{"disambiguationData":[OSD([sQuery(id+"F8.wireOp",EDGE,"E44.bottom"),sQuery(id+"F8.wireOp",EDGE,"E44.top"),sQuery(id+"F8.wireOp",EDGE,"E44.left"),sQuery(id+"F8.wireOp",EDGE,"E44.right")])]}),"instanceName":"39"});
            var Q40;
            Q40=makeQuery(id+"F1.opExtrude","SWEPT_BODY",BODY,{"disambiguationData":[OSD([sQuery(id+"F0.wireOp",EDGE,"E1")])]});
            booleanBodies(context, id + "F11", {"operationType" : BooleanOperationType.SUBTRACTION, "tools" : qUnion([Q0, Q1, Q2, Q3, Q4, Q5, Q6, Q7, Q8, Q9, Q10, Q11, Q12, Q13, Q14, Q15, Q16, Q17, Q18, Q19, Q20, Q21, Q22, Q23, Q24, Q25, Q26, Q27, Q28, Q29, Q30, Q31, Q32, Q33, Q34, Q35, Q36, Q37, Q38, Q39]), "targets" : qUnion([Q40])});
        }
        {
            var Q0;
            Q0=makeQuery(id+"F1.opExtrude","CAP_EDGE",EDGE,{"disambiguationData":[OSD([sQuery(id+"F0.wireOp",EDGE,"E1")])],"isStart":false});
            var Q1;
            Q1=makeQuery(id+"F3.opShell","OFFSET_EDGE",EDGE,{"disambiguationData":[OSD([sQuery(id+"F0.wireOp",EDGE,"E1")])]});
            fillet(context, id + "F12", {"entities" : qUnion([Q0, Q1]), "radius" : 20 * mm, "tangentPropagation" : true, "allowEdgeOverflow" : false});
        }
        {
            var Q0;
            Q0=makeQuery(id+"F2.opExtrude","CAP_FACE",FACE,{"disambiguationData":[OSD([sQuery(id+"F0.wireOp",EDGE,"E0"),sQuery(id+"F0.wireOp",EDGE,"E1")])],"isStart":false});
            var sketch = newSketch(context, id + "F13", { "sketchPlane" : qUnion([Q0])});
            skLineSegment(sketch, "E49", {"start": v(124.63, -18.56) * mm, "end": v(18.56, -124.63) * mm});
            skLineSegment(sketch, "E50", {"start": v(85.29, -99.43) * mm, "end": v(99.43, -85.29) * mm});
            skSolve(sketch);
        }
        {
            var Q0;
            {var subQ12=sQuery(id+"F13.wireOp",EDGE,"E49");Q0=makeQuery(id+"F13.imprint","IMPRINT",FACE,{"disambiguationData":[TD([[makeQuery(id+"F13.imprint","IMPRINT",EDGE,{"derivedFrom":subQ12}),1.0]])]});}
            extrude(context, id + "F14", {"entities" : qUnion([Q0]), "operationType" : NewBodyOperationType.ADD, "oppositeDirection" : true, "depth" : 155 * mm, "hasSecondDirection" : true, "secondDirectionOppositeDirection" : true, "secondDirectionDepth" : 69 * mm});
        }
        {
            var Q0;
            Q0=makeQuery(id+"F2.opExtrude","CAP_FACE",FACE,{"disambiguationData":[OSD([sQuery(id+"F0.wireOp",EDGE,"E0"),sQuery(id+"F0.wireOp",EDGE,"E1")])],"isStart":false});
            var sketch = newSketch(context, id + "F15", { "sketchPlane" : qUnion([Q0])});
            skLineSegment(sketch, "E51", {"start": v(121.73, -7.06) * mm, "end": v(6.13, -122.66) * mm});
            skLineSegment(sketch, "E52", {"start": v(10, -125.6) * mm, "end": v(6.13, -122.66) * mm});
            skLineSegment(sketch, "E53", {"start": v(125.6, -10) * mm, "end": v(121.73, -7.06) * mm});
            skLineSegment(sketch, "E54", {"start": v(10, -125.6) * mm, "end": v(10, -118.8) * mm});
            skLineSegment(sketch, "E55", {"start": v(125.6, -10) * mm, "end": v(118.8, -10) * mm});
            skSolve(sketch);
        }
        {
            var Q0;
            {var subQ4=sQuery(id+"F15.wireOp",EDGE,"E54");Q0=makeQuery(id+"F15.imprint","IMPRINT",FACE,{"disambiguationData":[TD([[makeQuery(id+"F15.imprint","IMPRINT",EDGE,{"derivedFrom":subQ4}),-1.0]])]});}
            var Q1;
            {var subQ0=sQuery(id+"F15.wireOp",EDGE,"E52");Q1=makeQuery(id+"F15.imprint","IMPRINT",FACE,{"disambiguationData":[TD([[makeQuery(id+"F15.imprint","IMPRINT",EDGE,{"derivedFrom":subQ0}),-1.0]])]});}
            var Q2;
            {var subQ0=sQuery(id+"F15.wireOp",EDGE,"E53");Q2=makeQuery(id+"F15.imprint","IMPRINT",FACE,{"disambiguationData":[TD([[makeQuery(id+"F15.imprint","IMPRINT",EDGE,{"derivedFrom":subQ0}),1.0]])]});}
            extrude(context, id + "F16", {"entities" : qUnion([Q0, Q1, Q2]), "operationType" : NewBodyOperationType.ADD, "oppositeDirection" : true, "depth" : 69 * mm});
        }
        {
            var Q0;
            Q0=makeQuery(id+"F16.opExtrude","SWEPT_FACE",FACE,{"disambiguationData":[OSD([sQuery(id+"F15.wireOp",EDGE,"E51")])]});
            var sketch = newSketch(context, id + "F17", { "sketchPlane" : qUnion([Q0])});
            skLineSegment(sketch, "E56.bottom", {"start": v(-81.09, 130.49) * mm, "end": v(77.91, 130.49) * mm});
            skLineSegment(sketch, "E56.top", {"start": v(-81.09, 175.19) * mm, "end": v(77.91, 175.19) * mm});
            skLineSegment(sketch, "E56.left", {"start": v(-81.09, 130.49) * mm, "end": v(-81.09, 175.19) * mm});
            skLineSegment(sketch, "E56.right", {"start": v(77.91, 130.49) * mm, "end": v(77.91, 175.19) * mm});
            skSolve(sketch);
        }
        {
            var Q0;
            Q0 = qSketchRegion(id + "F17", true);
            extrude(context, id + "F18", {"entities" : qUnion([Q0]), "operationType" : NewBodyOperationType.REMOVE, "endBound" : BoundingType.THROUGH_ALL, "oppositeDirection" : true, "depth" : 25 * mm});
        }
        {
            var Q0;
            Q0=makeQuery(id+"F14.opExtrude","SWEPT_FACE",FACE,{"disambiguationData":[OSD([sQuery(id+"F13.wireOp",EDGE,"E49")])]});
            var sketch = newSketch(context, id + "F19", { "sketchPlane" : qUnion([Q0])});
            skLineSegment(sketch, "E57.bottom", {"start": v(-66, 56.5) * mm, "end": v(-17, 56.5) * mm});
            skLineSegment(sketch, "E57.top", {"start": v(-66, 82.5) * mm, "end": v(-17, 82.5) * mm});
            skLineSegment(sketch, "E57.left", {"start": v(-66, 56.5) * mm, "end": v(-66, 82.5) * mm});
            skLineSegment(sketch, "E57.right", {"start": v(-17, 56.5) * mm, "end": v(-17, 82.5) * mm});
            skCircle(sketch, "E58", {"center": v(70, 106) * mm, "radius": 1.5 * mm});
            skCircle(sketch, "E59", {"center": v(-70, 106) * mm, "radius": 1.5 * mm});
            skLineSegment(sketch, "E60", {"start": v(70, 106) * mm, "end": v(75, 106) * mm});
            skLineSegment(sketch, "E61", {"start": v(70, 106) * mm, "end": v(70, 111) * mm});
            skLineSegment(sketch, "E62", {"start": v(-70, 106) * mm, "end": v(-75, 106) * mm});
            skCircle(sketch, "E63", {"center": v(-70, 106) * mm, "radius": 2.95 * mm});
            skCircle(sketch, "E64", {"center": v(70, 106) * mm, "radius": 2.95 * mm});
            skSolve(sketch);
        }
        {
            var Q0;
            Q0=makeQuery(id+"F19.imprint","IMPRINT",FACE,{"disambiguationData":[TD([[makeQuery(id+"F19.imprint","IMPRINT",EDGE,{"derivedFrom":sQuery(id+"F19.wireOp",EDGE,"E57.bottom")}),1.0]])]});
            var Q1;
            Q1=makeQuery(id+"F19.imprint","IMPRINT",FACE,{"disambiguationData":[TD([[makeQuery(id+"F19.imprint","IMPRINT",EDGE,{"derivedFrom":sQuery(id+"F19.wireOp",EDGE,"E59")}),1.0]])]});
            var Q2;
            {var subQ0=sQuery(id+"F19.wireOp",EDGE,"E60");var subQ1=sQuery(id+"F19.wireOp",EDGE,"E58");var subQ2=makeQuery(id+"F19.imprint","INTERSECT",VERTEX,{"derivedFrom":[subQ1,subQ0]});Q2=makeQuery(id+"F19.imprint","IMPRINT",FACE,{"disambiguationData":[TD([[makeQuery(id+"F19.imprint","IMPRINT",EDGE,{"disambiguationData":[TD([[subQ2,1.0]])],"derivedFrom":subQ1}),1.0]])]});}
            var Q3;
            {var subQ0=sQuery(id+"F19.wireOp",EDGE,"E60");var subQ1=sQuery(id+"F19.wireOp",EDGE,"E58");var subQ2=makeQuery(id+"F19.imprint","INTERSECT",VERTEX,{"derivedFrom":[subQ1,subQ0]});Q3=makeQuery(id+"F19.imprint","IMPRINT",FACE,{"disambiguationData":[TD([[makeQuery(id+"F19.imprint","IMPRINT",EDGE,{"disambiguationData":[TD([[subQ2,-1.0]])],"derivedFrom":subQ1}),1.0]])]});}
            extrude(context, id + "F20", {"entities" : qUnion([Q0, Q1, Q2, Q3]), "operationType" : NewBodyOperationType.REMOVE, "endBound" : BoundingType.THROUGH_ALL, "oppositeDirection" : true, "depth" : 25 * mm});
        }
        {
            var Q0;
            Q0=makeQuery(id+"F19.imprint","IMPRINT",FACE,{"disambiguationData":[TD([[makeQuery(id+"F19.imprint","IMPRINT",EDGE,{"derivedFrom":sQuery(id+"F19.wireOp",EDGE,"E59")}),-1.0]])]});
            var Q1;
            {var subQ0=sQuery(id+"F19.wireOp",EDGE,"E60");var subQ1=sQuery(id+"F19.wireOp",EDGE,"E58");var subQ2=makeQuery(id+"F19.imprint","INTERSECT",VERTEX,{"derivedFrom":[subQ1,subQ0]});Q1=makeQuery(id+"F19.imprint","IMPRINT",FACE,{"disambiguationData":[TD([[makeQuery(id+"F19.imprint","IMPRINT",EDGE,{"disambiguationData":[TD([[subQ2,-1.0]])],"derivedFrom":subQ1}),-1.0]])]});}
            var Q2;
            {var subQ0=sQuery(id+"F19.wireOp",EDGE,"E60");var subQ1=sQuery(id+"F19.wireOp",EDGE,"E58");var subQ2=makeQuery(id+"F19.imprint","INTERSECT",VERTEX,{"derivedFrom":[subQ1,subQ0]});Q2=makeQuery(id+"F19.imprint","IMPRINT",FACE,{"disambiguationData":[TD([[makeQuery(id+"F19.imprint","IMPRINT",EDGE,{"disambiguationData":[TD([[subQ2,1.0]])],"derivedFrom":subQ1}),-1.0]])]});}
            extrude(context, id + "F21", {"entities" : qUnion([Q0, Q1, Q2]), "operationType" : NewBodyOperationType.REMOVE, "oppositeDirection" : true, "depth" : 30 * mm, "hasSecondDirection" : true, "secondDirectionOppositeDirection" : true, "secondDirectionDepth" : 5 * mm});
        }
    });
